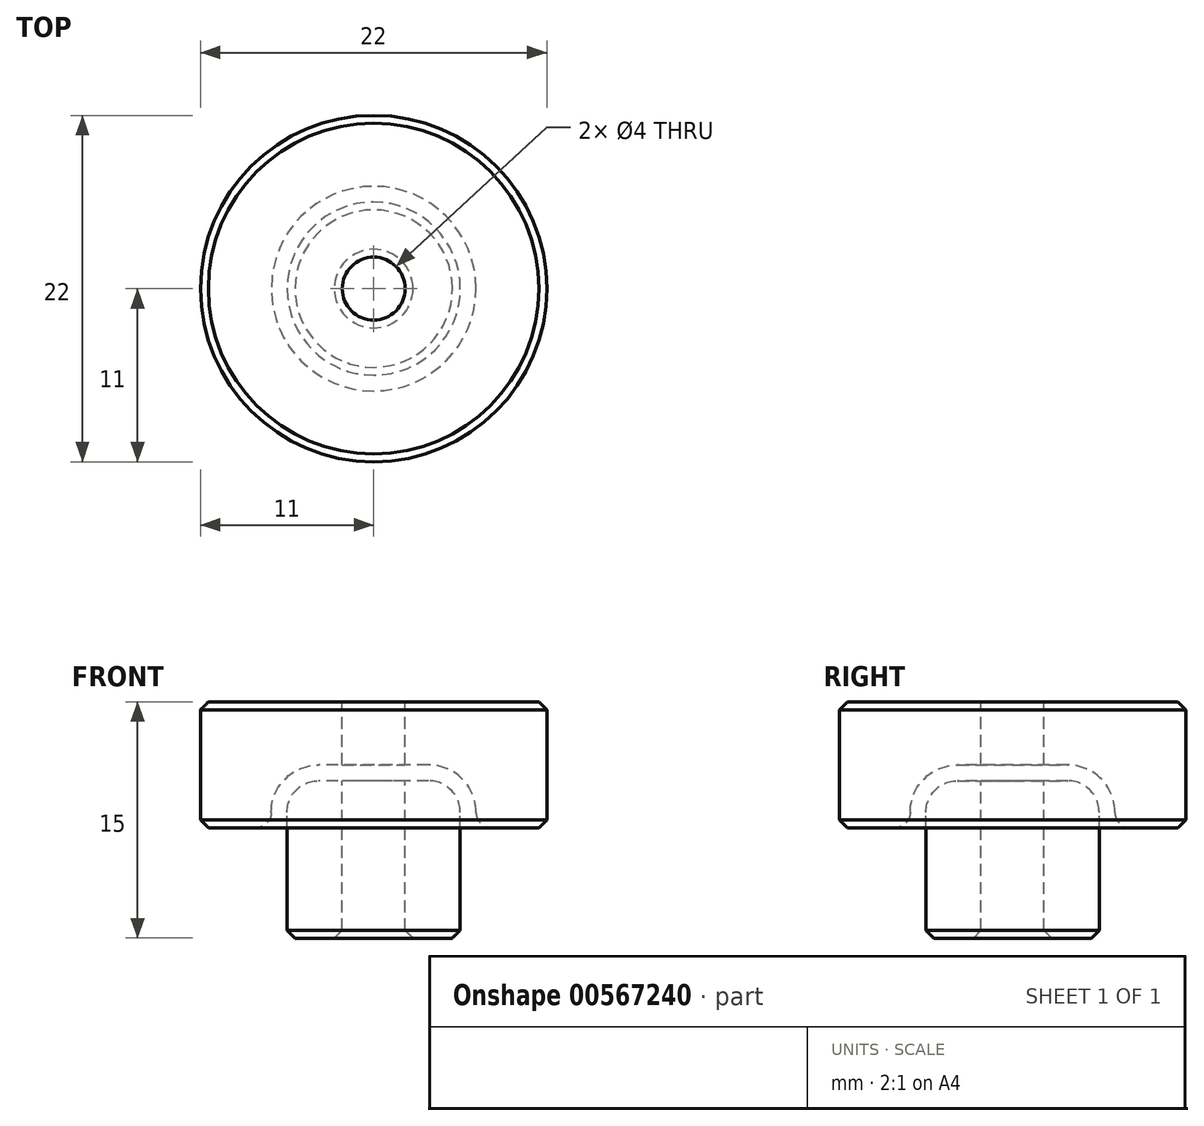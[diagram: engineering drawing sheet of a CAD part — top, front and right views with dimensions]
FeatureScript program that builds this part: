
annotation { "Feature Type Name" : "Feature", "Feature Type Description" : "" }
export const myFeature = defineFeature(function(context is Context, id is Id, definition is map)
    precondition{}
    {
        {
            var Q0;
            Q0=qCreatedBy(makeId("Front.planeOp"),FACE);
            var sketch = newSketch(context, id + "F0", { "sketchPlane" : qUnion([Q0])});
            skLineSegment(sketch, "E0", {"start": v(0, 10.49) * mm, "end": v(0, 0.49) * mm});
            skLineSegment(sketch, "E1", {"start": v(0, 0.49) * mm, "end": v(5.5, 0.49) * mm});
            skLineSegment(sketch, "E2", {"start": v(5.5, 0.49) * mm, "end": v(5.5, 8.49) * mm});
            skLineSegment(sketch, "E3", {"start": v(3.5, 10.49) * mm, "end": v(0, 10.49) * mm});
            skPoint(sketch, "E4.visualSharp", {"position": v(5.5, 10.49) * mm});
            skArc(sketch, "E4.filletArc", {"start": v(5.5, 8.49) * mm, "mid": v(4.91, 9.9) * mm, "end": v(3.5, 10.49) * mm});
            skLineSegment(sketch, "E5.0", {"start": v(3.5, 11.49) * mm, "end": v(0, 11.49) * mm});
            skArc(sketch, "E5.1", {"start": v(6.5, 8.49) * mm, "mid": v(5.62, 10.6) * mm, "end": v(3.5, 11.49) * mm});
            skLineSegment(sketch, "E6", {"start": v(6.5, 7.49) * mm, "end": v(11, 7.49) * mm});
            skLineSegment(sketch, "E7", {"start": v(11, 7.49) * mm, "end": v(11, 15.49) * mm});
            skLineSegment(sketch, "E8", {"start": v(11, 15.49) * mm, "end": v(0, 15.49) * mm});
            skLineSegment(sketch, "E9", {"start": v(0, 15.49) * mm, "end": v(0, 11.49) * mm});
            skLineSegment(sketch, "E10", {"start": v(6.5, 8.49) * mm, "end": v(6.5, 7.49) * mm});
            skSolve(sketch);
        }
        {
            var Q0;
            Q0=makeQuery(id+"F0.imprint","IMPRINT",FACE,{"disambiguationData":[TD([[makeQuery(id+"F0.imprint","IMPRINT",EDGE,{"derivedFrom":sQuery(id+"F0.wireOp",EDGE,"E0")}),1.0]])]});
            var Q1;
            Q1=makeQuery(id+"F0.imprint","IMPRINT",FACE,{"disambiguationData":[TD([[makeQuery(id+"F0.imprint","IMPRINT",EDGE,{"derivedFrom":sQuery(id+"F0.wireOp",EDGE,"E5.0")}),-1.0]])]});
            var Q2;
            Q2=sQuery(id+"F0.wireOp",EDGE,"E0");
            revolve(context, id + "F1", {"entities" : qUnion([Q0, Q1]), "axis" : qUnion([Q2]), "revolveType" : RevolveType.FULL});
        }
        {
            var Q0;
            Q0=makeQuery(id+"F1.opRevolve","SWEPT_FACE",FACE,{"disambiguationData":[OSD([sQuery(id+"F0.wireOp",EDGE,"E3")])]});
            var sketch = newSketch(context, id + "F2", { "sketchPlane" : qUnion([Q0])});
            skCircle(sketch, "E11", {"center": v(0, 0) * mm, "radius": 2 * mm});
            skSolve(sketch);
        }
        {
            var Q0;
            Q0=makeQuery(id+"F2.imprint","IMPRINT",FACE,{"disambiguationData":[TD([[makeQuery(id+"F2.imprint","IMPRINT",EDGE,{"derivedFrom":sQuery(id+"F2.wireOp",EDGE,"E11")}),1.0]])]});
            extrude(context, id + "F3", {"entities" : qUnion([Q0]), "operationType" : NewBodyOperationType.REMOVE, "endBound" : BoundingType.THROUGH_ALL, "oppositeDirection" : true, "depth" : 25 * mm, "offsetDistance" : 25 * mm});
        }
        {
            var Q0;
            Q0=makeQuery(id+"F1.opRevolve","SWEPT_EDGE",EDGE,{"disambiguationData":[OSD([sQuery(id+"F0.wireOp",EDGE,"E1"),sQuery(id+"F0.wireOp",EDGE,"E2")])]});
            var Q1;
            Q1=makeQuery(id+"F3.boolean.opBoolean","INTERSECT",EDGE,{"derivedFrom":[makeQuery(id+"F1.opRevolve","SWEPT_FACE",FACE,{"disambiguationData":[OSD([sQuery(id+"F0.wireOp",EDGE,"E1")])]}),makeQuery(id+"F3.opExtrude","SWEPT_FACE",FACE,{"disambiguationData":[OSD([sQuery(id+"F2.wireOp",EDGE,"E11")])]})]});
            chamfer(context, id + "F4", {"entities" : qUnion([Q0, Q1]), "width" : 0.5 * mm, "tangentPropagation" : true});
        }
        {
            var Q0;
            Q0=makeQuery(id+"F1.opRevolve","SWEPT_FACE",FACE,{"disambiguationData":[OSD([sQuery(id+"F0.wireOp",EDGE,"E8")])]});
            var sketch = newSketch(context, id + "F5", { "sketchPlane" : qUnion([Q0])});
            skCircle(sketch, "E12", {"center": v(0, 0) * mm, "radius": 2 * mm});
            skSolve(sketch);
        }
        {
            var Q0;
            Q0=makeQuery(id+"F5.imprint","IMPRINT",FACE,{"disambiguationData":[TD([[makeQuery(id+"F5.imprint","IMPRINT",EDGE,{"derivedFrom":sQuery(id+"F5.wireOp",EDGE,"E12")}),1.0]])]});
            extrude(context, id + "F6", {"entities" : qUnion([Q0]), "operationType" : NewBodyOperationType.REMOVE, "oppositeDirection" : true, "depth" : 25 * mm, "offsetDistance" : 25 * mm});
        }
        {
            var Q0;
            Q0=makeQuery(id+"F1.opRevolve","SWEPT_EDGE",EDGE,{"disambiguationData":[OSD([sQuery(id+"F0.wireOp",EDGE,"E6"),sQuery(id+"F0.wireOp",EDGE,"E7")])]});
            var Q1;
            Q1=makeQuery(id+"F1.opRevolve","SWEPT_EDGE",EDGE,{"disambiguationData":[OSD([sQuery(id+"F0.wireOp",EDGE,"E7"),sQuery(id+"F0.wireOp",EDGE,"E8")])]});
            var Q2;
            Q2=makeQuery(id+"F6.boolean.opBoolean","COPY",EDGE,{"derivedFrom":makeQuery(id+"F6.opExtrude","CAP_EDGE",EDGE,{"disambiguationData":[OSD([sQuery(id+"F5.wireOp",EDGE,"E12")])],"isStart":true})});
            chamfer(context, id + "F7", {"entities" : qUnion([Q0, Q1, Q2]), "width" : .5 * mm, "tangentPropagation" : true});
        }
        {
            var Q0;
            Q0=makeQuery(id+"F1.opRevolve","SWEPT_EDGE",EDGE,{"disambiguationData":[OSD([sQuery(id+"F0.wireOp",EDGE,"E6"),sQuery(id+"F0.wireOp",EDGE,"E10")])]});
            fillet(context, id + "F8", {"entities" : qUnion([Q0]), "radius" : 1 * mm, "tangentPropagation" : true, "allowEdgeOverflow" : false});
        }
    });
